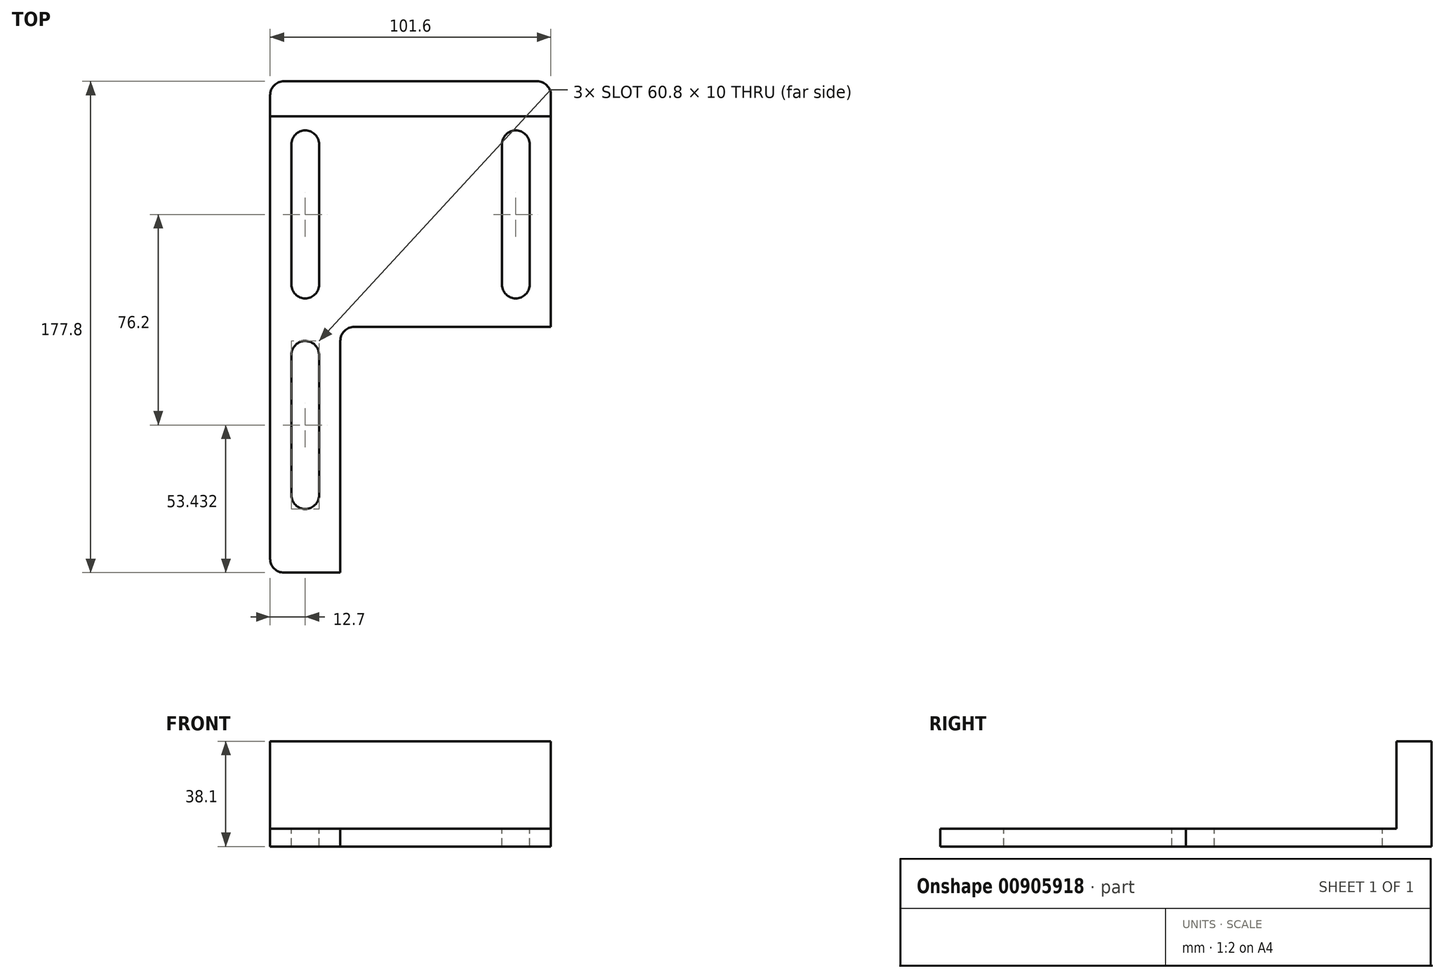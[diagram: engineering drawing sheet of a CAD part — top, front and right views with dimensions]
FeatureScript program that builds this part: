
annotation { "Feature Type Name" : "Feature", "Feature Type Description" : "" }
export const myFeature = defineFeature(function(context is Context, id is Id, definition is map)
    precondition{}
    {
        {
            var Q0;
            Q0=qCreatedBy(makeId("Top.planeOp"),FACE);
            var sketch = newSketch(context, id + "F0", { "sketchPlane" : qUnion([Q0])});
            skLineSegment(sketch, "E0.bottom", {"start": v(50.8, -88.9) * mm, "end": v(-50.8, -88.9) * mm});
            skLineSegment(sketch, "E0.top", {"start": v(50.8, 88.9) * mm, "end": v(-50.8, 88.9) * mm});
            skLineSegment(sketch, "E0.left", {"start": v(50.8, -88.9) * mm, "end": v(50.8, 88.9) * mm});
            skLineSegment(sketch, "E0.right", {"start": v(-50.8, -88.9) * mm, "end": v(-50.8, 88.9) * mm});
            skLineSegment(sketch, "E1.top", {"start": v(50.8, 76.2) * mm, "end": v(-50.8, 76.2) * mm});
            skLineSegment(sketch, "E1.left", {"start": v(50.8, 88.9) * mm, "end": v(50.8, 76.2) * mm});
            skLineSegment(sketch, "E1.right", {"start": v(-50.8, 88.9) * mm, "end": v(-50.8, 76.2) * mm});
            skLineSegment(sketch, "E2", {"start": v(-33.1, -10.1) * mm, "end": v(-33.1, -60.87) * mm});
            skLineSegment(sketch, "E3", {"start": v(-43.1, -10.07) * mm, "end": v(-43.1, -60.87) * mm});
            skArc(sketch, "E4", {"start": v(-43.1, -10.07) * mm, "mid": v(-38.08, -5.07) * mm, "end": v(-33.1, -10.1) * mm});
            skArc(sketch, "E5", {"start": v(-43.1, -60.87) * mm, "mid": v(-38.1, -65.87) * mm, "end": v(-33.1, -60.87) * mm});
            skLineSegment(sketch, "E6.bottom", {"start": v(-33.1, 15.33) * mm, "end": v(-43.1, 15.33) * mm});
            skLineSegment(sketch, "E6.top", {"start": v(-33.1, 66.13) * mm, "end": v(-43.1, 66.13) * mm});
            skLineSegment(sketch, "E6.left", {"start": v(-33.1, 15.33) * mm, "end": v(-33.1, 66.13) * mm});
            skLineSegment(sketch, "E6.right", {"start": v(-43.1, 15.33) * mm, "end": v(-43.1, 66.13) * mm});
            skPoint(sketch, "E6.middle", {"position": v(-38.1, 40.73) * mm});
            skLineSegment(sketch, "E7.bottom", {"start": v(43.1, 15.33) * mm, "end": v(33.1, 15.33) * mm});
            skLineSegment(sketch, "E7.top", {"start": v(43.1, 66.13) * mm, "end": v(33.1, 66.13) * mm});
            skLineSegment(sketch, "E7.left", {"start": v(43.1, 15.33) * mm, "end": v(43.1, 66.13) * mm});
            skLineSegment(sketch, "E7.right", {"start": v(33.1, 15.33) * mm, "end": v(33.1, 66.13) * mm});
            skPoint(sketch, "E7.middle", {"position": v(38.1, 40.73) * mm});
            skCircle(sketch, "E8", {"center": v(-38.1, 66.13) * mm, "radius": 5 * mm});
            skCircle(sketch, "E9", {"center": v(-38.1, 15.33) * mm, "radius": 5 * mm});
            skCircle(sketch, "E10", {"center": v(38.1, 15.33) * mm, "radius": 5 * mm});
            skCircle(sketch, "E11", {"center": v(38.1, 66.13) * mm, "radius": 5 * mm});
            skLineSegment(sketch, "E12.bottom", {"start": v(33.33, -10.75) * mm, "end": v(43.33, -10.75) * mm});
            skLineSegment(sketch, "E12.top", {"start": v(33.33, -61.55) * mm, "end": v(43.33, -61.55) * mm});
            skLineSegment(sketch, "E12.left", {"start": v(33.33, -10.75) * mm, "end": v(33.33, -61.55) * mm});
            skLineSegment(sketch, "E12.right", {"start": v(43.33, -10.75) * mm, "end": v(43.33, -61.55) * mm});
            skPoint(sketch, "E12.middle", {"position": v(38.33, -36.15) * mm});
            skArc(sketch, "E13", {"start": v(43.33, -10.75) * mm, "mid": v(38.33, -5.75) * mm, "end": v(33.33, -10.75) * mm});
            skArc(sketch, "E14", {"start": v(33.33, -61.55) * mm, "mid": v(38.33, -66.55) * mm, "end": v(43.33, -61.55) * mm});
            skLineSegment(sketch, "E15", {"start": v(-43.1, -10.07) * mm, "end": v(-50.8, -10.07) * mm});
            skLineSegment(sketch, "E16", {"start": v(43.33, -10.75) * mm, "end": v(50.8, -10.75) * mm});
            skLineSegment(sketch, "E17", {"start": v(-50.8, -88.9) * mm, "end": v(-25.4, -88.9) * mm});
            skLineSegment(sketch, "E18", {"start": v(-25.4, -88.9) * mm, "end": v(-25.4, 0) * mm});
            skLineSegment(sketch, "E19", {"start": v(-25.4, 0) * mm, "end": v(50.8, 0) * mm});
            skSolve(sketch);
        }
        {
            var Q0;
            Q0 = qSketchRegion(id + "F0", true);
            extrude(context, id + "F1", {"entities" : qUnion([Q0]), "depth" : -6.4 * mm, "offsetDistance" : 25 * mm});
        }
        {
            var Q0;
            Q0=makeQuery(id+"F0.imprint","IMPRINT",FACE,{"disambiguationData":[TD([[makeQuery(id+"F0.imprint","IMPRINT",EDGE,{"derivedFrom":sQuery(id+"F0.wireOp",EDGE,"E0.top")}),1.0]])]});
            extrude(context, id + "F2", {"entities" : qUnion([Q0]), "operationType" : NewBodyOperationType.ADD, "depth" : 31.7 * mm, "offsetDistance" : 25 * mm});
        }
        {
            var Q0;
            {var subQ3=sQuery(id+"F0.wireOp",EDGE,"E0.bottom");Q0=makeQuery(id+"F0.imprint","IMPRINT",FACE,{"disambiguationData":[TD([[makeQuery(id+"F0.imprint","IMPRINT",EDGE,{"derivedFrom":subQ3}),-1.0]])]});}
            extrude(context, id + "F3", {"entities" : qUnion([Q0]), "operationType" : NewBodyOperationType.REMOVE, "oppositeDirection" : true, "depth" : 6.4 * mm, "offsetDistance" : 25 * mm});
        }
        {
            var Q0;
            Q0=makeQuery(id+"F2.opExtrude","CAP_EDGE",EDGE,{"disambiguationData":[OSD([sQuery(id+"F0.wireOp",EDGE,"E1.top")])],"isStart":true});
            var Q1;
            {var subQ0=sQuery(id+"F0.wireOp",EDGE,"E1.left");var subQ1=sQuery(id+"F0.wireOp",EDGE,"E0.top");Q1=makeQuery(id+"F2.boolean.opBoolean","MERGE",EDGE,{"derivedFrom":[makeQuery(id+"F1.opExtrude","SWEPT_EDGE",EDGE,{"disambiguationData":[OSD([subQ1,subQ0])]}),makeQuery(id+"F2.opExtrude","SWEPT_EDGE",EDGE,{"disambiguationData":[OSD([subQ1,subQ0])]})]});}
            var Q2;
            {var subQ0=sQuery(id+"F0.wireOp",EDGE,"E1.right");var subQ1=sQuery(id+"F0.wireOp",EDGE,"E0.top");Q2=makeQuery(id+"F2.boolean.opBoolean","MERGE",EDGE,{"derivedFrom":[makeQuery(id+"F1.opExtrude","SWEPT_EDGE",EDGE,{"disambiguationData":[OSD([subQ1,subQ0])]}),makeQuery(id+"F2.opExtrude","SWEPT_EDGE",EDGE,{"disambiguationData":[OSD([subQ1,subQ0])]})]});}
            var Q3;
            Q3=makeQuery(id+"F3.boolean.opBoolean","COPY",EDGE,{"derivedFrom":makeQuery(id+"F3.opExtrude","SWEPT_EDGE",EDGE,{"disambiguationData":[OSD([sQuery(id+"F0.wireOp",EDGE,"E0.left"),sQuery(id+"F0.wireOp",EDGE,"E19")])]})});
            var Q4;
            Q4=makeQuery(id+"F3.boolean.opBoolean","COPY",EDGE,{"derivedFrom":makeQuery(id+"F3.opExtrude","SWEPT_EDGE",EDGE,{"disambiguationData":[OSD([sQuery(id+"F0.wireOp",EDGE,"E18"),sQuery(id+"F0.wireOp",EDGE,"E19")])]})});
            var Q5;
            Q5=makeQuery(id+"F3.boolean.opBoolean","COPY",EDGE,{"derivedFrom":makeQuery(id+"F3.opExtrude","SWEPT_EDGE",EDGE,{"disambiguationData":[OSD([sQuery(id+"F0.wireOp",EDGE,"E0.bottom"),sQuery(id+"F0.wireOp",EDGE,"E17"),sQuery(id+"F0.wireOp",EDGE,"E18")])]})});
            var Q6;
            Q6=makeQuery(id+"F1.opExtrude","SWEPT_EDGE",EDGE,{"disambiguationData":[OSD([sQuery(id+"F0.wireOp",EDGE,"E0.right"),sQuery(id+"F0.wireOp",EDGE,"E17")])]});
            fillet(context, id + "F4", {"entities" : qUnion([Q0, Q1, Q2, Q3, Q4, Q5, Q6]), "radius" : 5 * mm, "tangentPropagation" : true, "allowEdgeOverflow" : false});
        }
    });
